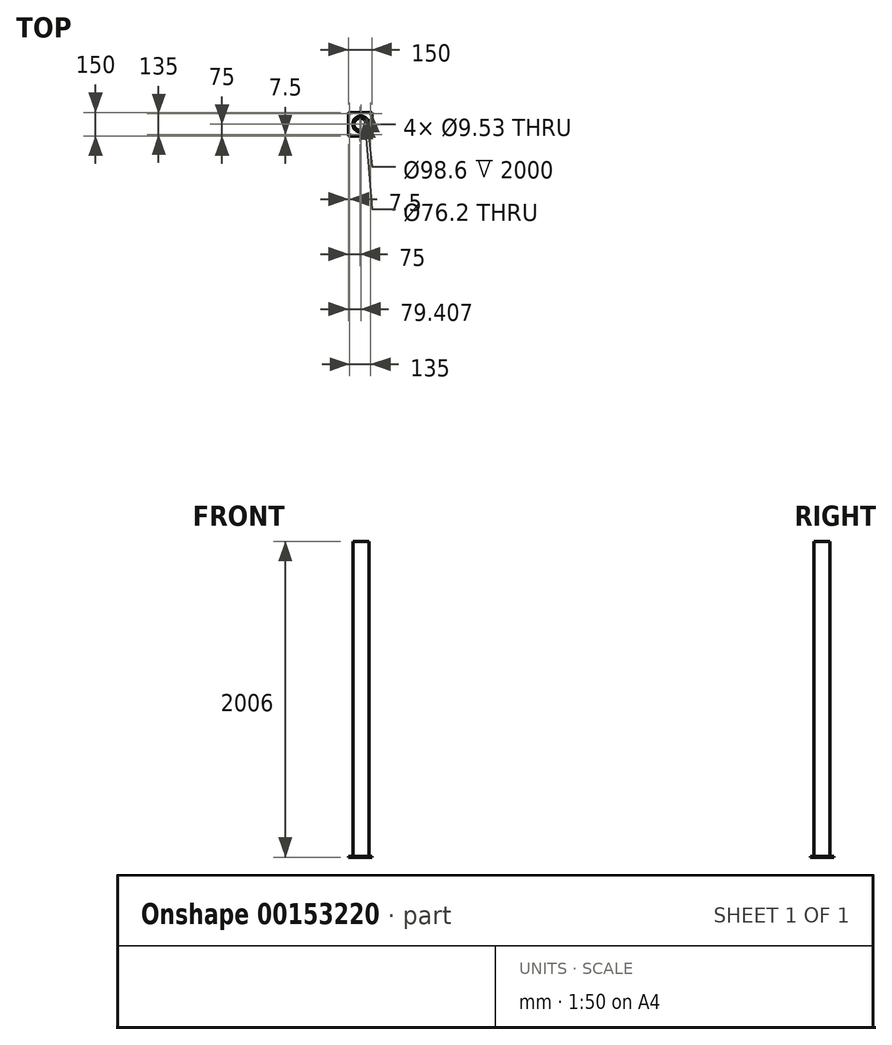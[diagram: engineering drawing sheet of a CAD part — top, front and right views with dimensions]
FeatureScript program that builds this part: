
annotation { "Feature Type Name" : "Feature", "Feature Type Description" : "" }
export const myFeature = defineFeature(function(context is Context, id is Id, definition is map)
    precondition{}
    {
        {
            var Q0;
            Q0=qCreatedBy(makeId("Top.planeOp"),FACE);
            var sketch = newSketch(context, id + "F0", { "sketchPlane" : qUnion([Q0])});
            skLineSegment(sketch, "E0.bottom", {"start": v(-75, 75) * mm, "end": v(75, 75) * mm});
            skLineSegment(sketch, "E0.top", {"start": v(-75, -75) * mm, "end": v(75, -75) * mm});
            skLineSegment(sketch, "E0.left", {"start": v(-75, 75) * mm, "end": v(-75, -75) * mm});
            skLineSegment(sketch, "E0.right", {"start": v(75, 75) * mm, "end": v(75, -75) * mm});
            skPoint(sketch, "E0.middle", {"position": v(0, 0) * mm});
            skCircle(sketch, "E1", {"center": v(0, 0) * mm, "radius": 38.1 * mm});
            skLineSegment(sketch, "E2.bottom", {"start": v(-67.5, -67.5) * mm, "end": v(67.5, -67.5) * mm});
            skLineSegment(sketch, "E2.top", {"start": v(-67.5, 67.5) * mm, "end": v(67.5, 67.5) * mm});
            skLineSegment(sketch, "E2.left", {"start": v(-67.5, -67.5) * mm, "end": v(-67.5, 67.5) * mm});
            skLineSegment(sketch, "E2.right", {"start": v(67.5, -67.5) * mm, "end": v(67.5, 67.5) * mm});
            skCircle(sketch, "E3", {"center": v(-67.5, -67.5) * mm, "radius": 4.76 * mm});
            skCircle(sketch, "E4.1.0.0", {"center": v(67.5, -67.5) * mm, "radius": 4.76 * mm});
            skCircle(sketch, "E4.2.0.0", {"center": v(202.5, -67.5) * mm, "radius": 4.76 * mm});
            skLineSegment(sketch, "E4.direction1", {"start": v(-67.5, -67.5) * mm, "end": v(67.5, -67.5) * mm, "construction": true});
            skCircle(sketch, "E5", {"center": v(-67.5, 67.5) * mm, "radius": 4.76 * mm});
            skCircle(sketch, "E6", {"center": v(67.5, 67.5) * mm, "radius": 4.76 * mm});
            skSolve(sketch);
        }
        {
            var Q0;
            Q0 = qSketchRegion(id + "F0", true);
            var Q1;
            Q1=makeQuery(id+"F0.imprint","IMPRINT",FACE,{"disambiguationData":[TD([[makeQuery(id+"F0.imprint","IMPRINT",EDGE,{"derivedFrom":sQuery(id+"F0.wireOp",EDGE,"E1")}),-1.0]])]});
            extrude(context, id + "F1", {"entities" : qUnion([Q0, Q1]), "depth" : 6 * mm});
        }
        {
            var Q0;
            Q0=makeQuery(id+"F1.opExtrude","CAP_FACE",FACE,{"disambiguationData":[OSD([sQuery(id+"F0.wireOp",EDGE,"E0.bottom"),sQuery(id+"F0.wireOp",EDGE,"E0.top"),sQuery(id+"F0.wireOp",EDGE,"E0.left"),sQuery(id+"F0.wireOp",EDGE,"E0.right"),sQuery(id+"F0.wireOp",EDGE,"E1"),sQuery(id+"F0.wireOp",EDGE,"E3"),sQuery(id+"F0.wireOp",EDGE,"E4.1.0.0"),sQuery(id+"F0.wireOp",EDGE,"E5"),sQuery(id+"F0.wireOp",EDGE,"E6")])],"isStart":false});
            var sketch = newSketch(context, id + "F2", { "sketchPlane" : qUnion([Q0])});
            skCircle(sketch, "E7", {"center": v(4.4, 0) * mm, "radius": 50.8 * mm});
            skCircle(sketch, "E8", {"center": v(4.4, 0) * mm, "radius": 49.3 * mm});
            skSolve(sketch);
        }
        {
            var Q0;
            Q0=makeQuery(id+"F1.opExtrude","SWEPT_BODY",BODY,{"disambiguationData":[OSD([sQuery(id+"F0.wireOp",EDGE,"E4.2.0.0")])]});
            deleteBodies(context, id + "F3", {"entities" : qUnion([Q0])});
        }
        {
            var Q0;
            Q0 = qSketchRegion(id + "F2", true);
            extrude(context, id + "F4", {"entities" : qUnion([Q0]), "depth" : 2000 * mm});
        }
    });
